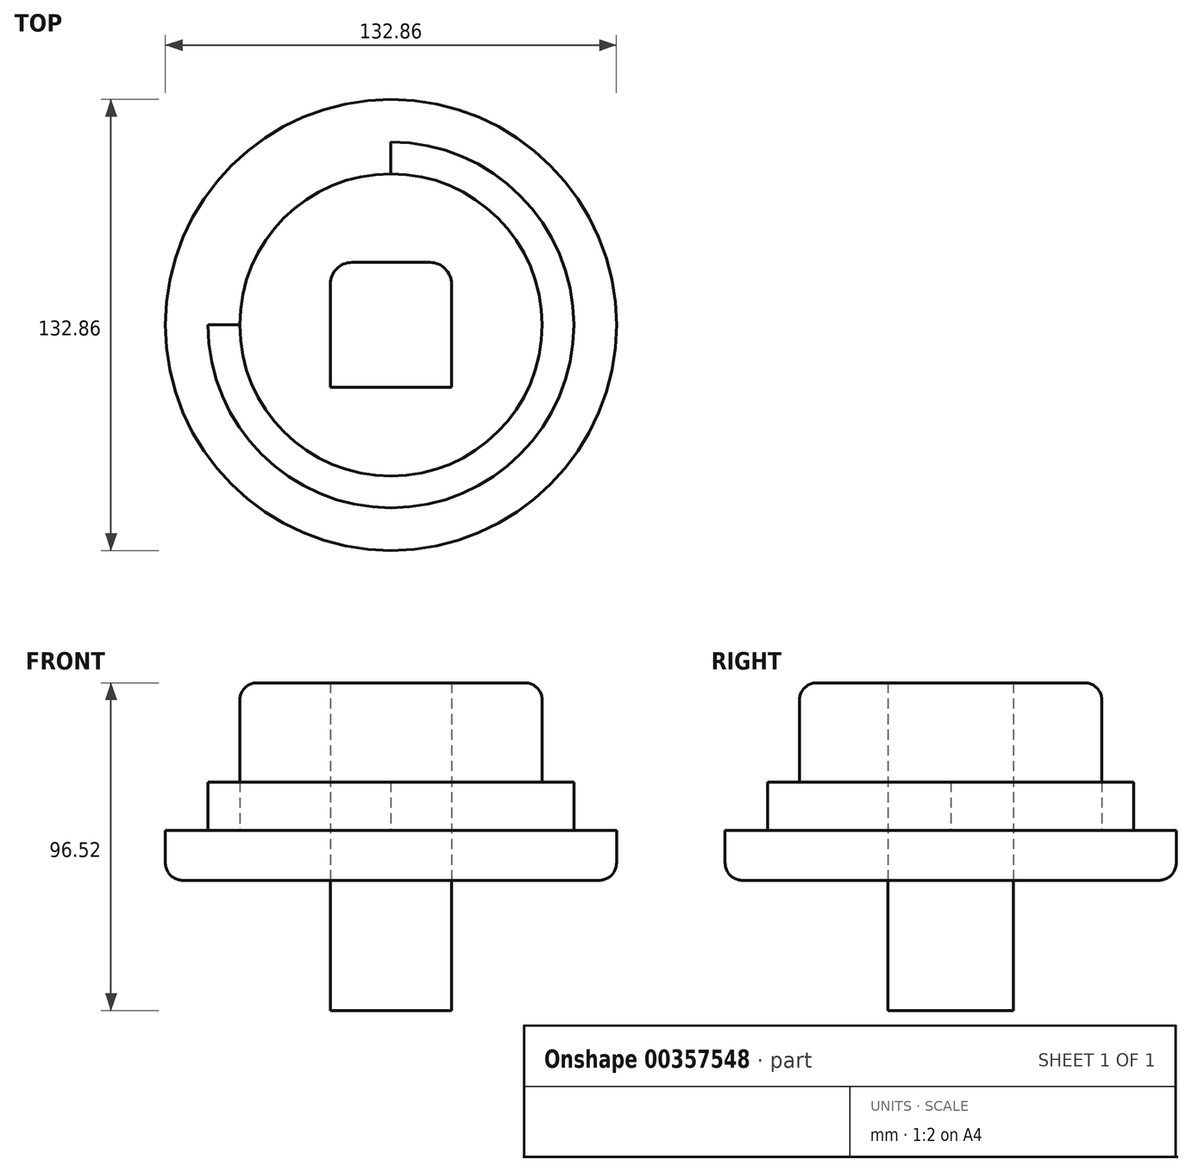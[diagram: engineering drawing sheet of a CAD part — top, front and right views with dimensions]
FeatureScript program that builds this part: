
annotation { "Feature Type Name" : "Feature", "Feature Type Description" : "" }
export const myFeature = defineFeature(function(context is Context, id is Id, definition is map)
    precondition{}
    {
        {
            var Q0;
            Q0=qCreatedBy(makeId("Top.planeOp"),FACE);
            var sketch = newSketch(context, id + "F0", { "sketchPlane" : qUnion([Q0])});
            skCircle(sketch, "E0", {"center": v(0, 0) * mm, "radius": 44.54 * mm});
            skLineSegment(sketch, "E1.bottom", {"start": v(-11.5, 18.42) * mm, "end": v(11.5, 18.42) * mm});
            skLineSegment(sketch, "E1.top", {"start": v(-17.84, -18.42) * mm, "end": v(17.84, -18.42) * mm});
            skLineSegment(sketch, "E1.left", {"start": v(-17.84, 12.07) * mm, "end": v(-17.84, -18.42) * mm});
            skLineSegment(sketch, "E1.right", {"start": v(17.84, 12.07) * mm, "end": v(17.84, -18.42) * mm});
            skPoint(sketch, "E2.visualSharp", {"position": v(17.84, 18.42) * mm});
            skArc(sketch, "E2.filletArc", {"start": v(17.84, 12.07) * mm, "mid": v(15.98, 16.56) * mm, "end": v(11.5, 18.42) * mm});
            skPoint(sketch, "E3.visualSharp", {"position": v(-17.84, 18.42) * mm});
            skArc(sketch, "E3.filletArc", {"start": v(-11.5, 18.42) * mm, "mid": v(-15.98, 16.56) * mm, "end": v(-17.84, 12.07) * mm});
            skArc(sketch, "E4", {"start": v(-53.87, 0) * mm, "mid": v(38.1, -38.1) * mm, "end": v(0, 53.87) * mm});
            skCircle(sketch, "E5", {"center": v(0, 0) * mm, "radius": 66.43 * mm});
            skLineSegment(sketch, "E6", {"start": v(0, 53.87) * mm, "end": v(0, 44.54) * mm});
            skLineSegment(sketch, "E7", {"start": v(-53.87, 0) * mm, "end": v(-44.54, 0) * mm});
            skSolve(sketch);
        }
        {
            var Q0;
            Q0=makeQuery(id+"F0.imprint","IMPRINT",FACE,{"disambiguationData":[TD([[makeQuery(id+"F0.imprint","IMPRINT",EDGE,{"derivedFrom":sQuery(id+"F0.wireOp",EDGE,"E0")}),1.0]])]});
            extrude(context, id + "F1", {"entities" : qUnion([Q0]), "depth" : 58.17 * mm});
        }
        {
            var Q0;
            Q0=makeQuery(id+"F0.imprint","IMPRINT",FACE,{"disambiguationData":[TD([[makeQuery(id+"F0.imprint","IMPRINT",EDGE,{"derivedFrom":sQuery(id+"F0.wireOp",EDGE,"E4")}),1.0]])]});
            extrude(context, id + "F2", {"entities" : qUnion([Q0]), "operationType" : NewBodyOperationType.ADD, "depth" : 28.96 * mm});
        }
        {
            var Q0;
            Q0=makeQuery(id+"F0.imprint","IMPRINT",FACE,{"disambiguationData":[TD([[makeQuery(id+"F0.imprint","IMPRINT",EDGE,{"derivedFrom":sQuery(id+"F0.wireOp",EDGE,"E4")}),-1.0]])]});
            extrude(context, id + "F3", {"entities" : qUnion([Q0]), "operationType" : NewBodyOperationType.ADD, "depth" : 14.73 * mm});
        }
        {
            var Q0;
            Q0=makeQuery(id+"F0.imprint","IMPRINT",FACE,{"disambiguationData":[TD([[makeQuery(id+"F0.imprint","IMPRINT",EDGE,{"derivedFrom":sQuery(id+"F0.wireOp",EDGE,"E1.bottom")}),-1.0]])]});
            extrude(context, id + "F4", {"entities" : qUnion([Q0]), "oppositeDirection" : true, "depth" : 38.35 * mm});
        }
        {
            var Q0;
            Q0=makeQuery(id+"F3.opExtrude","CAP_EDGE",EDGE,{"disambiguationData":[OSD([sQuery(id+"F0.wireOp",EDGE,"E5")])],"isStart":true});
            fillet(context, id + "F5", {"entities" : qUnion([Q0]), "radius" : 5.08 * mm, "tangentPropagation" : true, "allowEdgeOverflow" : false});
        }
        {
            var Q0;
            Q0=makeQuery(id+"F1.opExtrude","CAP_EDGE",EDGE,{"disambiguationData":[OSD([sQuery(id+"F0.wireOp",EDGE,"E0")])],"isStart":false});
            fillet(context, id + "F6", {"entities" : qUnion([Q0]), "radius" : 5.08 * mm, "tangentPropagation" : true, "allowEdgeOverflow" : false});
        }
    });
